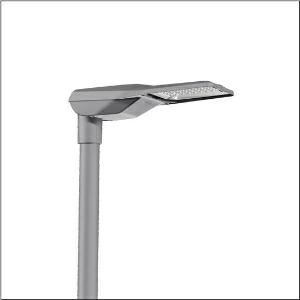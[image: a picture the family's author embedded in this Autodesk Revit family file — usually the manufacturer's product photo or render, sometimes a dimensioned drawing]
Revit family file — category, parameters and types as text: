
# Revit family: streetlight_sl_21_iq_mini___st0_8a_5xe2c31g08gb_0650
name_source: partatom
category: Lighting Fixtures
units: mm (PartAtom-declared; Revit-internal decimal feet)

## family parameters
Cut with Voids When Loaded = No
Host = Face
Light Source = No
Part Type = Normal
Room Calculation Point = No
Round Connector Dimension = Use Diameter
Shared = No

## types (1)
- --- (1 x LED, 5680 lm, 37.1 W, 3000K)
    Apparent Load = 37 VA
    CIE Flux Codes = 38 75 97 100 100
    Color Rendering = 70
    Color Temperature = 3000K
    Default Elevation = 1800 mm
    Description = Streetlight SL 21 iQ mini, mast luminaire, primary light control with lens, of PMMA, primary optical cover: cover, of toughened safety glass, transparent, light distribution: ST0.8a, light emission: direct distribution, primary light characteristic: asymmetric, installation type: post-top, side-entry, LED, High Power LED, rated luminous flux: 5.680lm, luminous efficacy: 153lm/W, light colour: 730, colour temperature: 3000K, control: Street-Remote, Auto-Match, Temp-Guard, Lumen-Switch, Night-Set, Smart-Wire, Light-Fading, Desk-Remote (wireless, voltage-free reading and setting of iQ features in the workshop via application-optimized NFC function/RFID function), optimised constant luminous flux control (CLO 2.0), presetting dimming linear, mains connection: 220..240V, AC, 50/60Hz, start of lifetime: 37W, end of service life: 39W, reduction: 18W, luminaire housing, of diecast aluminium, powder-coated, Siteco® metallic grey (DB 702S), corrosivity category C5 mid according to DIN EN ISO 12944, please order mast flange separately, inclination adjustable: 0°, 5°, 10°, 15°, sealing non-destructively replaceable, multi-level sealing system, length: 628mm, width: 235mm, height: 110mm, mast flange for spigot size: 42mm (side-entry): 5XC10008XM4, 60/48mm (side-entry/post-top): 5XC10108XM2, 76/60mm (side-entry/post-top): 5XC10108XM1, protection rating (complete): IP66, insulation class (complete): insulation class II (safety insulation), certification: CE, ENEC, ENEC+, VDE, impact resistance: IK09, permissible operating ambient temperature for outdoor applications: -40..+50°C, standard-compliant lighting for roads and squares, packaging unit: 1 piece

Light Distribution: ST0.8a
    Height = 110 mm
    Lamp = 1 x LED
    Lamp Light Flux = 5680 lm
    Lamp Power = 37.1 W
    Lamp count = 1
    Length = 625 mm
    Luminous efficacy = 153 lm/W
    Manufacturer = Siteco
    ModVariant = No
    Model = 5XE2C31G08GB
    Number of Poles = 1
    OnlyDefault = Yes
    Power Factor = 1
    Product Name = Streetlight SL 21 iQ mini | ST0.8a
    Product group = mast luminaire | pylon top
    ProductGroupID = 6100
    Protection Class = Protection class II
    Protection Degree = IP 66
    RLX_Detail_Level = 1
    RLX_Emergency_Light_Flux = 0 lm
    RLX_Emergency_Type = 0
    RLX_Emergency_Type_DB = No
    RlxData = <blob elided: 92873 chars, md5=502c27e8>
    Socket = socket
    Standby Power = 0 W
    System Light Flux = 5680 lm
    System Power = 37 W
    Type Comments = factory setting: luminous flux: 100 % | dim-lin: 254 | 385 mA
    Type Image = l_1003519.jpg
    URL = http://relux.com
    VarID = @adj_137281
    Voltage = 0 V
    Weight = 0.00 kg
    Width = 234 mm

## geometry (parser evidence)
native form markers: Blend x4, Sweep x9
no freeform markers — native parametric forms only
